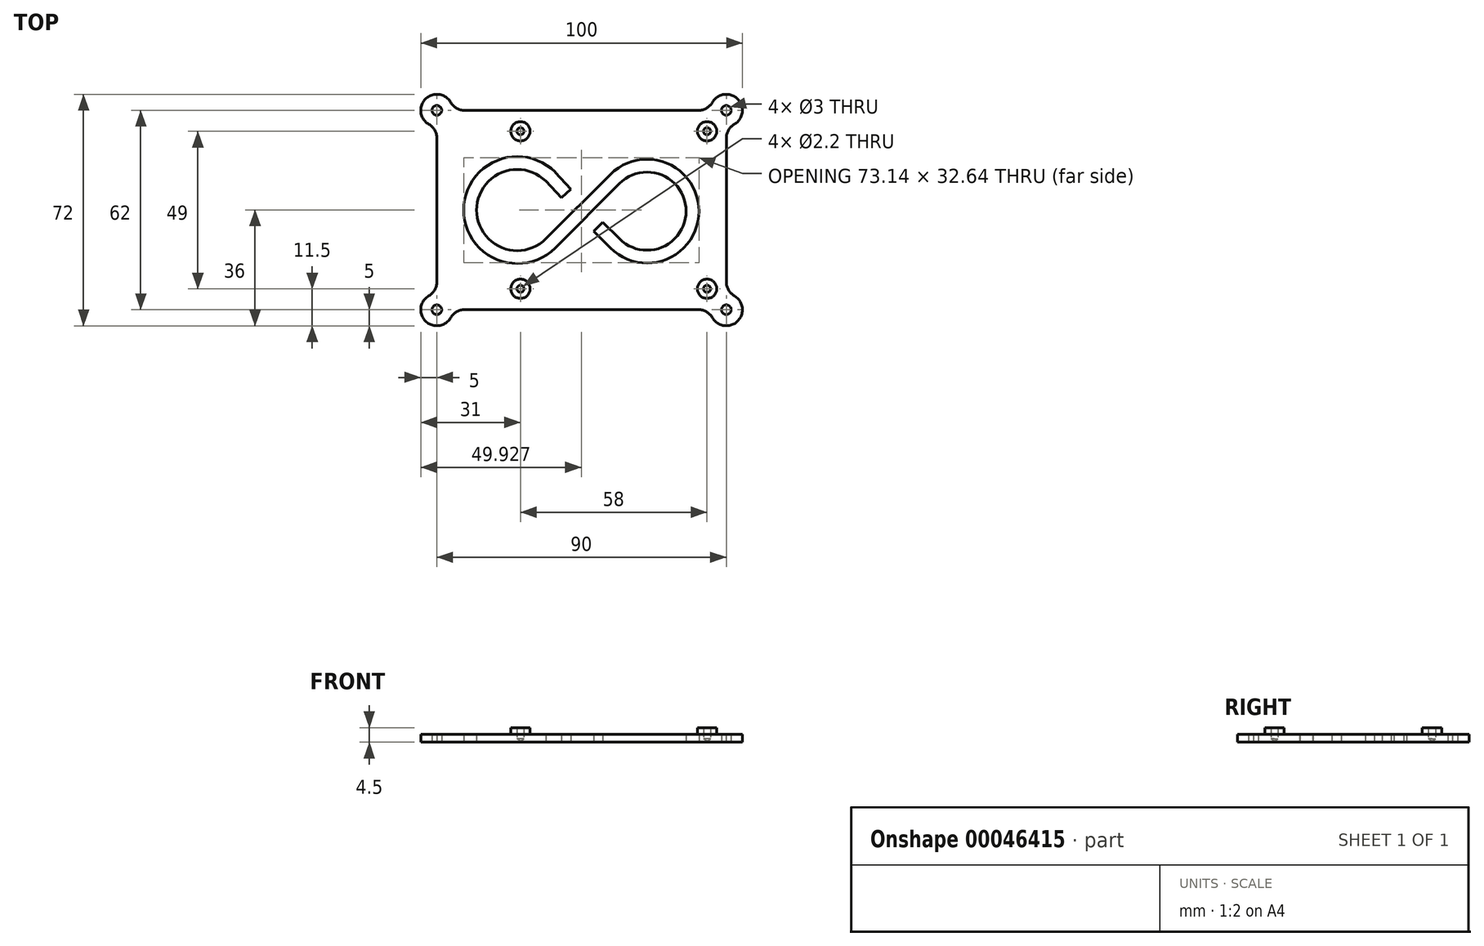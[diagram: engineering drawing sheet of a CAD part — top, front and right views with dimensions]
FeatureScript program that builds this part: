
annotation { "Feature Type Name" : "Feature", "Feature Type Description" : "" }
export const myFeature = defineFeature(function(context is Context, id is Id, definition is map)
    precondition{}
    {
        {
            var Q0;
            Q0=qCreatedBy(makeId("Top.planeOp"),FACE);
            var sketch = newSketch(context, id + "F0", { "sketchPlane" : qUnion([Q0])});
            skLineSegment(sketch, "E0.bottom", {"start": v(45, -31) * mm, "end": v(-45, -31) * mm});
            skLineSegment(sketch, "E0.top", {"start": v(45, 31) * mm, "end": v(-45, 31) * mm});
            skLineSegment(sketch, "E0.left", {"start": v(45, -31) * mm, "end": v(45, 31) * mm});
            skLineSegment(sketch, "E0.right", {"start": v(-45, -31) * mm, "end": v(-45, 31) * mm});
            skPoint(sketch, "E0.middle", {"position": v(0, 0) * mm});
            skCircle(sketch, "E1", {"center": v(45, 31) * mm, "radius": 5 * mm});
            skCircle(sketch, "E2", {"center": v(45, -31) * mm, "radius": 5 * mm});
            skCircle(sketch, "E3", {"center": v(-45, 31) * mm, "radius": 5 * mm});
            skCircle(sketch, "E4", {"center": v(-45, -31) * mm, "radius": 5 * mm});
            skCircle(sketch, "E5", {"center": v(45, 31) * mm, "radius": 1.5 * mm});
            skCircle(sketch, "E6", {"center": v(45, -31) * mm, "radius": 1.5 * mm});
            skCircle(sketch, "E7", {"center": v(-45, -31) * mm, "radius": 1.5 * mm});
            skCircle(sketch, "E8", {"center": v(-45, 31) * mm, "radius": 1.5 * mm});
            skPoint(sketch, "E9.third.point", {"position": v(34.14, 0) * mm});
            skPoint(sketch, "E9.third.point.positionSnap0", {"position": v(10, 0) * mm});
            skArc(sketch, "E10", {"start": v(10.35, 9.65) * mm, "mid": v(34.5, -0.35) * mm, "end": v(10.35, -10.35) * mm});
            skArc(sketch, "E11", {"start": v(-9.65, -10.35) * mm, "mid": v(-34.64, 0) * mm, "end": v(-9.65, 10.35) * mm});
            skLineSegment(sketch, "E12", {"start": v(-9.65, -10.35) * mm, "end": v(10.35, 9.65) * mm});
            skPoint(sketch, "E13", {"position": v(5.18, -5.18) * mm});
            skPoint(sketch, "E14", {"position": v(-4.82, 5.18) * mm});
            skLineSegment(sketch, "E15", {"start": v(-9.65, 10.35) * mm, "end": v(-4.82, 5.18) * mm});
            skLineSegment(sketch, "E16", {"start": v(10.35, -10.35) * mm, "end": v(5.18, -5.18) * mm});
            skArc(sketch, "E17.0.startCap", {"start": v(11.77, 8.23) * mm, "mid": v(8.94, 8.23) * mm, "end": v(8.94, 11.06) * mm});
            skArc(sketch, "E17.0.endCap", {"start": v(8.94, -11.77) * mm, "mid": v(8.94, -8.94) * mm, "end": v(11.77, -8.94) * mm});
            skArc(sketch, "E17.0.left", {"start": v(8.94, 11.06) * mm, "mid": v(36.5, -0.35) * mm, "end": v(8.94, -11.77) * mm});
            skArc(sketch, "E17.0.right", {"start": v(11.77, 8.23) * mm, "mid": v(32.5, -0.35) * mm, "end": v(11.77, -8.94) * mm});
            skArc(sketch, "E17.1.startCap", {"start": v(11.77, -8.94) * mm, "mid": v(11.77, -11.77) * mm, "end": v(8.94, -11.77) * mm});
            skLineSegment(sketch, "E17.1.left", {"start": v(8.94, -11.77) * mm, "end": v(3.76, -6.6) * mm});
            skLineSegment(sketch, "E17.1.right", {"start": v(11.77, -8.94) * mm, "end": v(6.6, -3.76) * mm});
            skArc(sketch, "E17.2.startCap", {"start": v(-8.23, -11.77) * mm, "mid": v(-11.06, -11.77) * mm, "end": v(-11.06, -8.94) * mm});
            skArc(sketch, "E17.2.endCap", {"start": v(8.94, 11.06) * mm, "mid": v(11.77, 11.06) * mm, "end": v(11.77, 8.23) * mm});
            skLineSegment(sketch, "E17.2.left", {"start": v(-11.06, -8.94) * mm, "end": v(8.94, 11.06) * mm});
            skLineSegment(sketch, "E17.2.right", {"start": v(-8.23, -11.77) * mm, "end": v(11.77, 8.23) * mm});
            skArc(sketch, "E17.3.startCap", {"start": v(-11.06, -8.94) * mm, "mid": v(-8.23, -8.94) * mm, "end": v(-8.23, -11.77) * mm});
            skArc(sketch, "E17.3.endCap", {"start": v(-8.23, 11.77) * mm, "mid": v(-8.23, 8.94) * mm, "end": v(-11.06, 8.94) * mm});
            skArc(sketch, "E17.3.left", {"start": v(-8.23, -11.77) * mm, "mid": v(-36.64, 0) * mm, "end": v(-8.23, 11.77) * mm});
            skArc(sketch, "E17.3.right", {"start": v(-11.06, -8.94) * mm, "mid": v(-32.64, 0) * mm, "end": v(-11.06, 8.94) * mm});
            skArc(sketch, "E17.4.startCap", {"start": v(-11.1, 9) * mm, "mid": v(-11, 11.82) * mm, "end": v(-8.18, 11.72) * mm});
            skLineSegment(sketch, "E17.4.left", {"start": v(-8.18, 11.72) * mm, "end": v(-3.36, 6.54) * mm});
            skLineSegment(sketch, "E17.4.right", {"start": v(-11.1, 9) * mm, "end": v(-6.29, 3.81) * mm});
            skLineSegment(sketch, "E18", {"start": v(-6.29, 3.81) * mm, "end": v(-3.36, 6.54) * mm});
            skLineSegment(sketch, "E19", {"start": v(3.76, -6.6) * mm, "end": v(6.6, -3.76) * mm});
            skSolve(sketch);
        }
        {
            var Q0;
            Q0 = qSketchRegion(id + "F0", true);
            extrude(context, id + "F1", {"entities" : qUnion([Q0]), "depth" : 2.5 * mm});
        }
        {
            var Q0;
            Q0=makeQuery(id+"F1.opExtrude","SWEPT_EDGE",EDGE,{"disambiguationData":[OSD([sQuery(id+"F0.wireOp",EDGE,"E0.bottom"),sQuery(id+"F0.wireOp",EDGE,"E4")])]});
            var Q1;
            Q1=makeQuery(id+"F1.opExtrude","SWEPT_EDGE",EDGE,{"disambiguationData":[OSD([sQuery(id+"F0.wireOp",EDGE,"E0.left"),sQuery(id+"F0.wireOp",EDGE,"E1")])]});
            var Q2;
            Q2=makeQuery(id+"F1.opExtrude","SWEPT_EDGE",EDGE,{"disambiguationData":[OSD([sQuery(id+"F0.wireOp",EDGE,"E0.bottom"),sQuery(id+"F0.wireOp",EDGE,"E2")])]});
            var Q3;
            Q3=makeQuery(id+"F1.opExtrude","SWEPT_EDGE",EDGE,{"disambiguationData":[OSD([sQuery(id+"F0.wireOp",EDGE,"E0.right"),sQuery(id+"F0.wireOp",EDGE,"E4")])]});
            var Q4;
            Q4=makeQuery(id+"F1.opExtrude","SWEPT_EDGE",EDGE,{"disambiguationData":[OSD([sQuery(id+"F0.wireOp",EDGE,"E0.right"),sQuery(id+"F0.wireOp",EDGE,"E3")])]});
            var Q5;
            Q5=makeQuery(id+"F1.opExtrude","SWEPT_EDGE",EDGE,{"disambiguationData":[OSD([sQuery(id+"F0.wireOp",EDGE,"E0.top"),sQuery(id+"F0.wireOp",EDGE,"E3")])]});
            var Q6;
            Q6=makeQuery(id+"F1.opExtrude","SWEPT_EDGE",EDGE,{"disambiguationData":[OSD([sQuery(id+"F0.wireOp",EDGE,"E0.top"),sQuery(id+"F0.wireOp",EDGE,"E1")])]});
            var Q7;
            Q7=makeQuery(id+"F1.opExtrude","SWEPT_EDGE",EDGE,{"disambiguationData":[OSD([sQuery(id+"F0.wireOp",EDGE,"E0.left"),sQuery(id+"F0.wireOp",EDGE,"E2")])]});
            fillet(context, id + "F2", {"entities" : qUnion([Q0, Q1, Q2, Q3, Q4, Q5, Q6, Q7]), "radius" : 5 * mm, "tangentPropagation" : true, "allowEdgeOverflow" : false});
        }
        {
            var Q0;
            Q0=makeQuery(id+"F1.opExtrude","CAP_FACE",FACE,{"disambiguationData":[OSD([sQuery(id+"F0.wireOp",EDGE,"E0.bottom"),sQuery(id+"F0.wireOp",EDGE,"E0.top"),sQuery(id+"F0.wireOp",EDGE,"E0.left"),sQuery(id+"F0.wireOp",EDGE,"E0.right"),sQuery(id+"F0.wireOp",EDGE,"E1"),sQuery(id+"F0.wireOp",EDGE,"E2"),sQuery(id+"F0.wireOp",EDGE,"E3"),sQuery(id+"F0.wireOp",EDGE,"E4"),sQuery(id+"F0.wireOp",EDGE,"E5"),sQuery(id+"F0.wireOp",EDGE,"E6"),sQuery(id+"F0.wireOp",EDGE,"E7"),sQuery(id+"F0.wireOp",EDGE,"E8"),sQuery(id+"F0.wireOp",EDGE,"E17.0.left"),sQuery(id+"F0.wireOp",EDGE,"E17.0.right"),sQuery(id+"F0.wireOp",EDGE,"E17.1.left"),sQuery(id+"F0.wireOp",EDGE,"E17.1.right"),sQuery(id+"F0.wireOp",EDGE,"E17.2.left"),sQuery(id+"F0.wireOp",EDGE,"E17.2.right"),sQuery(id+"F0.wireOp",EDGE,"E17.3.left"),sQuery(id+"F0.wireOp",EDGE,"E17.3.right"),sQuery(id+"F0.wireOp",EDGE,"E17.4.startCap"),sQuery(id+"F0.wireOp",EDGE,"E17.4.left"),sQuery(id+"F0.wireOp",EDGE,"E17.4.right"),sQuery(id+"F0.wireOp",EDGE,"E18"),sQuery(id+"F0.wireOp",EDGE,"E19")])],"isStart":false});
            var sketch = newSketch(context, id + "F3", { "sketchPlane" : qUnion([Q0])});
            skPoint(sketch, "E20", {"position": v(39, 24.5) * mm});
            skPoint(sketch, "E21", {"position": v(39, -24.5) * mm});
            skPoint(sketch, "E22", {"position": v(-19, 24.5) * mm});
            skPoint(sketch, "E23", {"position": v(-19, -24.5) * mm});
            skCircle(sketch, "E24", {"center": v(-19, 24.5) * mm, "radius": 3 * mm});
            skCircle(sketch, "E25", {"center": v(39, 24.5) * mm, "radius": 3 * mm});
            skCircle(sketch, "E26", {"center": v(39, -24.5) * mm, "radius": 3 * mm});
            skCircle(sketch, "E27", {"center": v(-19, -24.5) * mm, "radius": 3 * mm});
            skSolve(sketch);
        }
        {
            var Q0;
            Q0=makeQuery(id+"F3.imprint","IMPRINT",FACE,{"disambiguationData":[TD([[makeQuery(id+"F3.imprint","IMPRINT",EDGE,{"derivedFrom":sQuery(id+"F3.wireOp",EDGE,"E27")}),1.0]])]});
            var Q1;
            Q1=makeQuery(id+"F3.imprint","IMPRINT",FACE,{"disambiguationData":[TD([[makeQuery(id+"F3.imprint","IMPRINT",EDGE,{"derivedFrom":sQuery(id+"F3.wireOp",EDGE,"E26")}),1.0]])]});
            var Q2;
            Q2=makeQuery(id+"F3.imprint","IMPRINT",FACE,{"disambiguationData":[TD([[makeQuery(id+"F3.imprint","IMPRINT",EDGE,{"derivedFrom":sQuery(id+"F3.wireOp",EDGE,"E25")}),1.0]])]});
            var Q3;
            Q3=makeQuery(id+"F3.imprint","IMPRINT",FACE,{"disambiguationData":[TD([[makeQuery(id+"F3.imprint","IMPRINT",EDGE,{"derivedFrom":sQuery(id+"F3.wireOp",EDGE,"E24")}),1.0]])]});
            var Q4;
            Q4=sQuery(id+"F3.wireOp",EDGE,"E24");
            var Q5;
            Q5=sQuery(id+"F3.wireOp",EDGE,"E25");
            var Q6;
            Q6=sQuery(id+"F3.wireOp",EDGE,"E26");
            var Q7;
            Q7=sQuery(id+"F3.wireOp",EDGE,"E27");
            extrude(context, id + "F4", {"entities" : qUnion([Q0, Q1, Q2, Q3]), "operationType" : NewBodyOperationType.ADD, "surfaceEntities" : qUnion([Q4, Q5, Q6, Q7]), "depth" : 2 * mm});
        }
        {
            var Q0;
            Q0=makeQuery(id+"F4.opExtrude","CAP_FACE",FACE,{"disambiguationData":[OSD([sQuery(id+"F3.wireOp",EDGE,"E24")])],"isStart":false});
            var sketch = newSketch(context, id + "F5", { "sketchPlane" : qUnion([Q0])});
            skPoint(sketch, "E28", {"position": v(-19, 24.5) * mm});
            skPoint(sketch, "E29", {"position": v(-19, -24.5) * mm});
            skPoint(sketch, "E30", {"position": v(39, 24.5) * mm});
            skPoint(sketch, "E31", {"position": v(39, -24.5) * mm});
            skSolve(sketch);
        }
        {
            var Q0;
            Q0=sQuery(id+"F5.wireOp",VERTEX,"E28");
            var Q1;
            Q1=sQuery(id+"F5.wireOp",VERTEX,"E30");
            var Q2;
            Q2=sQuery(id+"F5.wireOp",VERTEX,"E31");
            var Q3;
            Q3=sQuery(id+"F5.wireOp",VERTEX,"E29");
            var Q4;
            Q4=makeQuery(id+"F1.opExtrude","SWEPT_BODY",BODY,{"disambiguationData":[OSD([sQuery(id+"F0.wireOp",EDGE,"E0.bottom"),sQuery(id+"F0.wireOp",EDGE,"E0.top"),sQuery(id+"F0.wireOp",EDGE,"E0.left"),sQuery(id+"F0.wireOp",EDGE,"E0.right"),sQuery(id+"F0.wireOp",EDGE,"E1"),sQuery(id+"F0.wireOp",EDGE,"E2"),sQuery(id+"F0.wireOp",EDGE,"E3"),sQuery(id+"F0.wireOp",EDGE,"E4"),sQuery(id+"F0.wireOp",EDGE,"E5"),sQuery(id+"F0.wireOp",EDGE,"E6"),sQuery(id+"F0.wireOp",EDGE,"E7"),sQuery(id+"F0.wireOp",EDGE,"E8"),sQuery(id+"F0.wireOp",EDGE,"E17.0.left"),sQuery(id+"F0.wireOp",EDGE,"E17.0.right"),sQuery(id+"F0.wireOp",EDGE,"E17.1.left"),sQuery(id+"F0.wireOp",EDGE,"E17.1.right"),sQuery(id+"F0.wireOp",EDGE,"E17.2.left"),sQuery(id+"F0.wireOp",EDGE,"E17.2.right"),sQuery(id+"F0.wireOp",EDGE,"E17.3.left"),sQuery(id+"F0.wireOp",EDGE,"E17.3.right"),sQuery(id+"F0.wireOp",EDGE,"E17.4.startCap"),sQuery(id+"F0.wireOp",EDGE,"E17.4.left"),sQuery(id+"F0.wireOp",EDGE,"E17.4.right"),sQuery(id+"F0.wireOp",EDGE,"E18"),sQuery(id+"F0.wireOp",EDGE,"E19")])]});
            hole(context, id + "F6", {"style" : HoleStyle.SIMPLE, "endStyle" : HoleEndStyle.BLIND, "holeDiameter" : 2.2 * mm, "holeDepth" : 3.5 * mm, "locations" : qUnion([Q0, Q1, Q2, Q3]), "scope" : qUnion([Q4]), "startStyle" : HoleStartStyle.PART});
        }
    });
